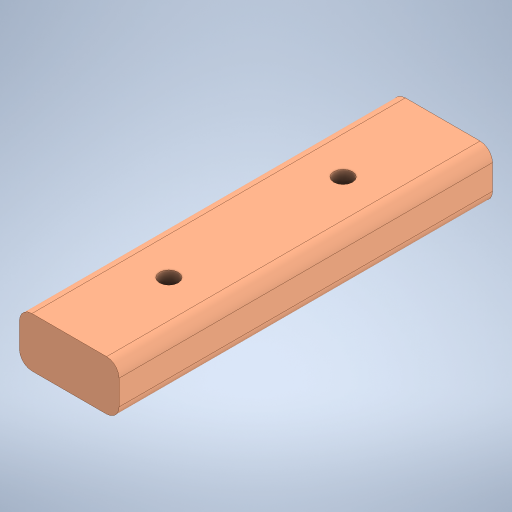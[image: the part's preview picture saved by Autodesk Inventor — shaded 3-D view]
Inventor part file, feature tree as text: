
AUTODESK INVENTOR PART (.ipt)
format: ipt  version: 2024 (Build 280153000, 153)  size: 245,760 bytes
history: native  units: mm
features: extrude x2
ambient origin geometry x8: Origin, YZ Plane, XZ Plane, XY Plane, X Axis, Y Axis, Z Axis, Center Point
bodies: Solid1 (feature_tree)
feature tree (2):
  extrude  "Extrusion1"  Depth=12.7mm
  extrude  "Extrusion2"  Depth=101.6mm
